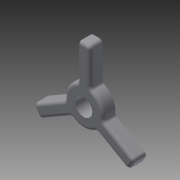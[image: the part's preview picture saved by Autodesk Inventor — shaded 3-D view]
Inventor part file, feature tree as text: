
AUTODESK INVENTOR PART (.ipt)
format: ipt  version: 2013 (Build 170138000, 138)  size: 159,744 bytes
history: native  units: in
note: dims shown in document units (in); Inventor stores cm internally (conversion verified against a paired STEP export)
features: extrude x1, pattern_circular x1, fillet x1, sketch x1
ambient origin geometry x8: Origin, YZ Plane, XZ Plane, XY Plane, X Axis, Y Axis, Z Axis, Center Point
bodies: Solid1 (feature_tree)
feature tree (4):
  extrude  "Extrusion1"  Depth=0.2362in
  pattern_circular  "Circular Pattern1"  [2 undecoded]
  fillet  "Fillet1"  Radius=0.3204in
  sketch  "Sketch1"  dims[d0=1.0305in d2=0.2362in d3=0.1969in d4=0.3204in d5=0.2362in d6=0.0in d7=1.1811in d8=360.0deg d10=0.0625in]
note: 2 required parameter values undecoded (feature->parameter linkage not recoverable at this tier; creation-order binding heuristic only, values carry confidence <= 0.55)
